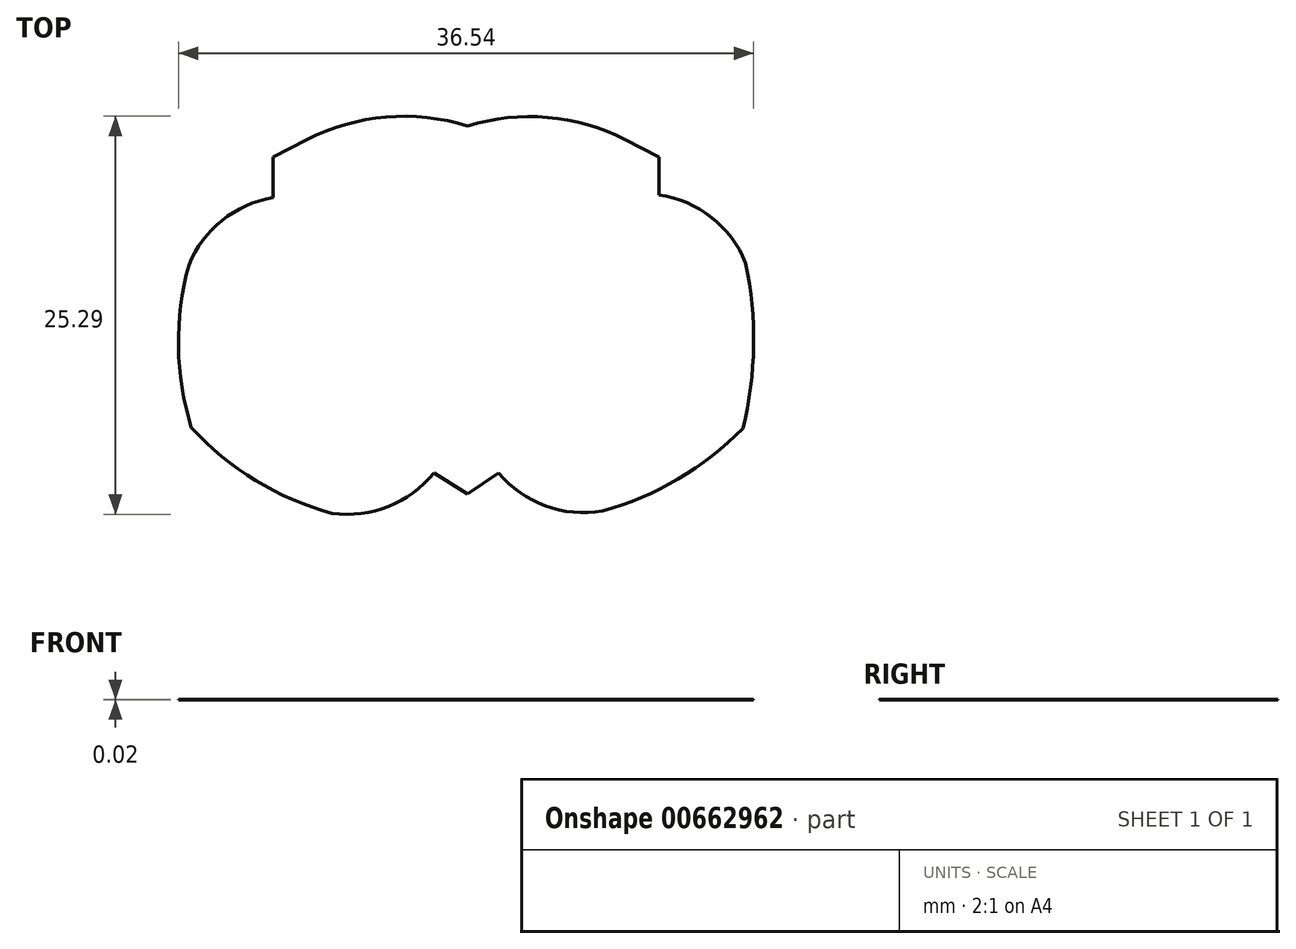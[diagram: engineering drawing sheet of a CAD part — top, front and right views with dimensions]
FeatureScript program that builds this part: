
annotation { "Feature Type Name" : "Feature", "Feature Type Description" : "" }
export const myFeature = defineFeature(function(context is Context, id is Id, definition is map)
    precondition{}
    {
        {
            var Q0;
            Q0=qCreatedBy(makeId("Top.planeOp"),FACE);
            var sketch = newSketch(context, id + "F0", { "sketchPlane" : qUnion([Q0])});
            skPoint(sketch, "E0.center", {"position": v(0, 0) * mm});
            skLineSegment(sketch, "E1", {"start": v(-10.2, 8.25) * mm, "end": v(-12.37, 7.15) * mm});
            skLineSegment(sketch, "E2", {"start": v(-12.37, 7.15) * mm, "end": v(-12.37, 4.64) * mm});
            skLineSegment(sketch, "E3.MirrorCS", {"start": v(12.16, 7.15) * mm, "end": v(12.16, 4.64) * mm});
            skLineSegment(sketch, "E4.MirrorCS", {"start": v(10, 8.25) * mm, "end": v(12.16, 7.15) * mm});
            skArc(sketch, "E5", {"start": v(17.66, 0.43) * mm, "mid": v(15.48, 3.32) * mm, "end": v(12.16, 4.74) * mm});
            skArc(sketch, "E6.MirrorCS", {"start": v(8.56, -15.34) * mm, "mid": v(4.94, -15) * mm, "end": v(1.97, -12.9) * mm});
            skLineSegment(sketch, "E7", {"start": v(1.97, -12.9) * mm, "end": v(0, -14.26) * mm});
            skLineSegment(sketch, "E8", {"start": v(0, -14.26) * mm, "end": v(-2.14, -12.9) * mm});
            skArc(sketch, "E9", {"start": v(-8.6, -15.48) * mm, "mid": v(-5.03, -15.05) * mm, "end": v(-2.14, -12.9) * mm});
            skArc(sketch, "E10.MirrorCS", {"start": v(-17.7, 0.28) * mm, "mid": v(-15.6, 3.12) * mm, "end": v(-12.37, 4.57) * mm});
            skLineSegment(sketch, "E11", {"start": v(-12.37, 4.64) * mm, "end": v(-12.37, 4.57) * mm});
            skArc(sketch, "E12", {"start": v(17.49, -10.1) * mm, "mid": v(18.17, -4.84) * mm, "end": v(17.66, 0.43) * mm});
            skArc(sketch, "E13", {"start": v(8.56, -15.34) * mm, "mid": v(13.37, -13.3) * mm, "end": v(17.49, -10.1) * mm});
            skArc(sketch, "E14", {"start": v(-17.7, 0.28) * mm, "mid": v(-18.36, -4.89) * mm, "end": v(-17.55, -10.04) * mm});
            skArc(sketch, "E15", {"start": v(-17.55, -10.04) * mm, "mid": v(-13.46, -13.4) * mm, "end": v(-8.6, -15.48) * mm});
            skArc(sketch, "E16", {"start": v(0, 9.12) * mm, "mid": v(-5.19, 9.69) * mm, "end": v(-10.2, 8.25) * mm});
            skArc(sketch, "E17", {"start": v(10, 8.25) * mm, "mid": v(5.08, 9.66) * mm, "end": v(0, 9.12) * mm});
            skSolve(sketch);
        }
        {
            var Q0;
            Q0=makeQuery(id+"F0.imprint","IMPRINT",FACE,{"disambiguationData":[TD([[makeQuery(id+"F0.imprint","IMPRINT",EDGE,{"derivedFrom":sQuery(id+"F0.wireOp",EDGE,"E1")}),1.0]])]});
            extrude(context, id + "F1", {"entities" : qUnion([Q0]), "depth" : 7.5 / 406.4 * mm, "offsetDistance" : 25.4 * mm});
        }
    });
